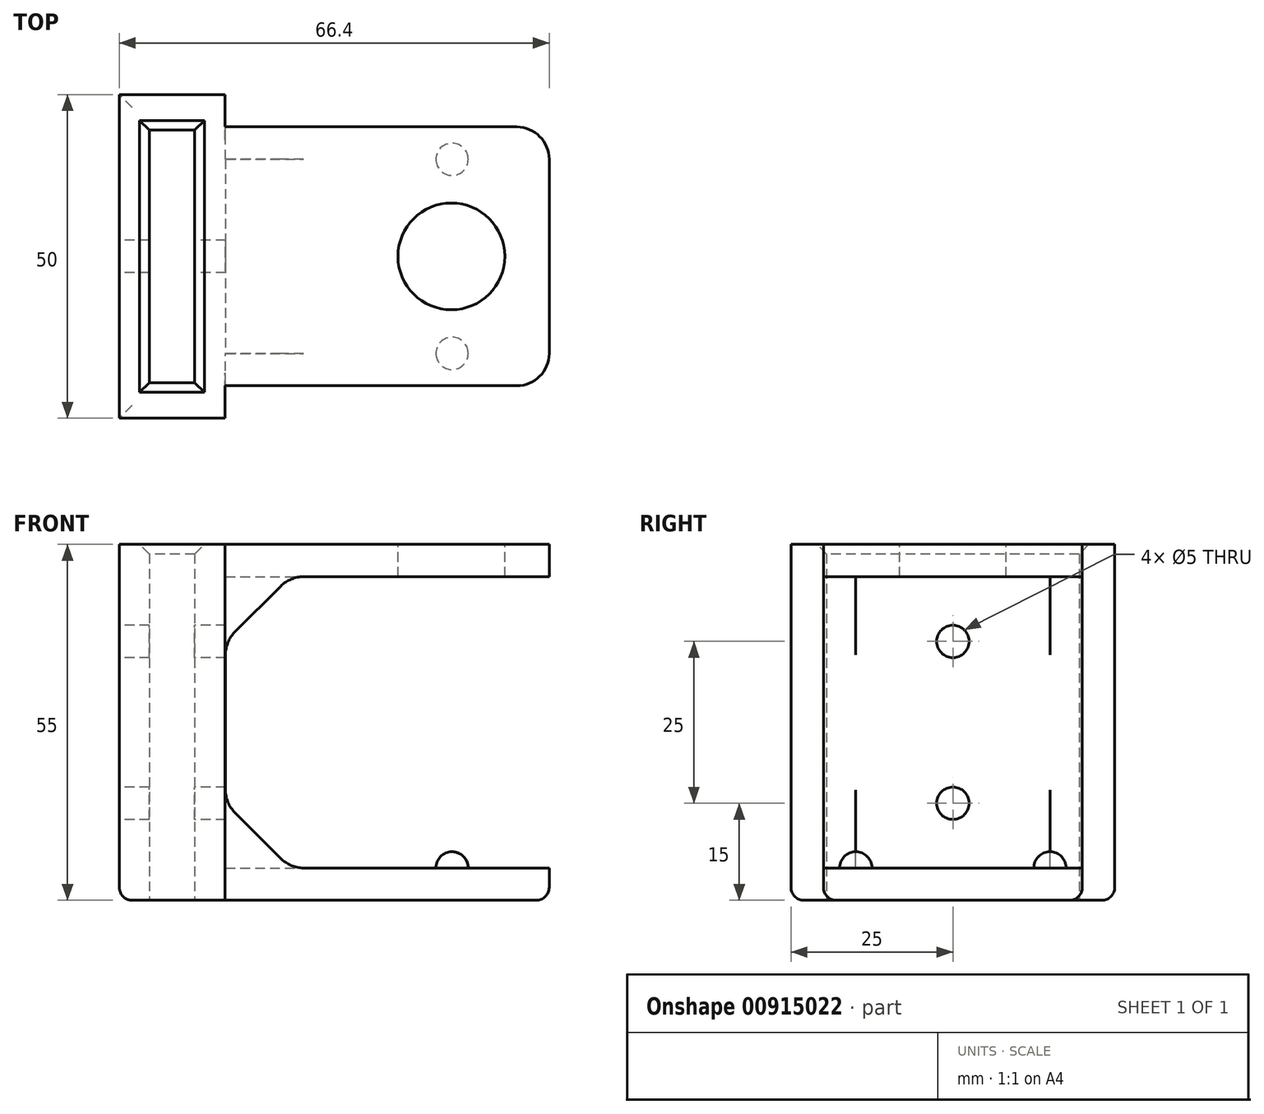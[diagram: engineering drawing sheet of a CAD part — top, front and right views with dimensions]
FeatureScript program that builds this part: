
annotation { "Feature Type Name" : "Feature", "Feature Type Description" : "" }
export const myFeature = defineFeature(function(context is Context, id is Id, definition is map)
    precondition{}
    {
        {
            var Q0;
            Q0=qCreatedBy(makeId("Front.planeOp"),FACE);
            var sketch = newSketch(context, id + "F0", { "sketchPlane" : qUnion([Q0])});
            skLineSegment(sketch, "E0", {"start": v(0, 0) * mm, "end": v(0, 55) * mm});
            skLineSegment(sketch, "E1", {"start": v(0, 55) * mm, "end": v(50.1, 55) * mm});
            skLineSegment(sketch, "E2", {"start": v(50.1, 55) * mm, "end": v(50.1, 50) * mm});
            skLineSegment(sketch, "E3", {"start": v(50.1, 50) * mm, "end": v(0.1, 50) * mm});
            skLineSegment(sketch, "E4", {"start": v(0.1, 50) * mm, "end": v(0.1, 5) * mm});
            skLineSegment(sketch, "E5", {"start": v(0.1, 5) * mm, "end": v(50.1, 5) * mm});
            skLineSegment(sketch, "E6", {"start": v(50.1, 5) * mm, "end": v(50.1, 0) * mm});
            skLineSegment(sketch, "E7", {"start": v(50.1, 0) * mm, "end": v(0, 0) * mm});
            skSolve(sketch);
        }
        {
            var Q0;
            Q0=makeQuery(id+"F0.imprint","IMPRINT",FACE,{"disambiguationData":[TD([[makeQuery(id+"F0.imprint","IMPRINT",EDGE,{"derivedFrom":sQuery(id+"F0.wireOp",EDGE,"E0")}),-1.0]])]});
            extrude(context, id + "F1", {"entities" : qUnion([Q0]), "oppositeDirection" : true, "depth" : 40 * mm, "offsetDistance" : 25 * mm});
        }
        {
            var Q0;
            Q0=makeQuery(id+"F1.opExtrude","SWEPT_FACE",FACE,{"disambiguationData":[OSD([sQuery(id+"F0.wireOp",EDGE,"E1")])]});
            var sketch = newSketch(context, id + "F2", { "sketchPlane" : qUnion([Q0])});
            skCircle(sketch, "E8", {"center": v(35, 20) * mm, "radius": 8.25 * mm});
            skPoint(sketch, "E8.centerSnap0", {"position": v(0, 20) * mm});
            skPoint(sketch, "E8.centerSnap1", {"position": v(25.05, 0) * mm});
            skSolve(sketch);
        }
        {
            var Q0;
            Q0=makeQuery(id+"F2.imprint","IMPRINT",FACE,{"disambiguationData":[TD([[makeQuery(id+"F2.imprint","IMPRINT",EDGE,{"derivedFrom":sQuery(id+"F2.wireOp",EDGE,"E8")}),1.0]])]});
            extrude(context, id + "F3", {"entities" : qUnion([Q0]), "operationType" : NewBodyOperationType.REMOVE, "endBound" : BoundingType.UP_TO_NEXT, "oppositeDirection" : true, "depth" : 25 * mm, "offsetDistance" : 25 * mm});
        }
        {
            var Q0;
            Q0=makeQuery(id+"F1.opExtrude","SWEPT_FACE",FACE,{"disambiguationData":[OSD([sQuery(id+"F0.wireOp",EDGE,"E0")])]});
            var sketch = newSketch(context, id + "F4", { "sketchPlane" : qUnion([Q0])});
            skLineSegment(sketch, "E9.bottom", {"start": v(5, 55) * mm, "end": v(-45, 55) * mm});
            skLineSegment(sketch, "E9.top", {"start": v(5, 0) * mm, "end": v(-45, 0) * mm});
            skLineSegment(sketch, "E9.left", {"start": v(5, 55) * mm, "end": v(5, 0) * mm});
            skLineSegment(sketch, "E9.right", {"start": v(-45, 55) * mm, "end": v(-45, 0) * mm});
            skPoint(sketch, "E9.middle", {"position": v(-20, 27.5) * mm});
            skPoint(sketch, "E9.middle.positionSnap0", {"position": v(-20, 55) * mm});
            skPoint(sketch, "E9.middle.positionSnap1", {"position": v(0, 27.5) * mm});
            skPoint(sketch, "E9.cornerSnap0", {"position": v(-20, 55) * mm});
            skPoint(sketch, "E9.centerSnap0", {"position": v(-20, 55) * mm});
            skPoint(sketch, "E9.centerSnap1", {"position": v(0, 27.5) * mm});
            skSolve(sketch);
        }
        {
            var Q0;
            {var subQ2=sQuery(id+"F4.wireOp",EDGE,"E9.left");Q0=makeQuery(id+"F4.imprint","IMPRINT",FACE,{"disambiguationData":[TD([[makeQuery(id+"F4.imprint","IMPRINT",EDGE,{"derivedFrom":subQ2}),-1.0]])]});}
            var Q1;
            {var subQ1=sQuery(id+"F0.wireOp",EDGE,"E0");var subQ2=makeQuery(id+"F1.opExtrude","CAP_EDGE",EDGE,{"disambiguationData":[OSD([subQ1])],"isStart":true});Q1=makeQuery(id+"F4.imprint","IMPRINT",FACE,{"disambiguationData":[TD([[makeQuery(id+"F4.imprint","IMPRINT",EDGE,{"derivedFrom":subQ2}),1.0]])]});}
            var Q2;
            {var subQ2=sQuery(id+"F4.wireOp",EDGE,"E9.right");Q2=makeQuery(id+"F4.imprint","IMPRINT",FACE,{"disambiguationData":[TD([[makeQuery(id+"F4.imprint","IMPRINT",EDGE,{"derivedFrom":subQ2}),1.0]])]});}
            extrude(context, id + "F5", {"entities" : qUnion([Q0, Q1, Q2]), "operationType" : NewBodyOperationType.ADD, "depth" : 16.3 * mm, "offsetDistance" : 25 * mm});
        }
        {
            var Q0;
            Q0=makeQuery(id+"F5.boolean.opBoolean","MERGE",FACE,{"derivedFrom":[makeQuery(id+"F1.opExtrude","SWEPT_FACE",FACE,{"disambiguationData":[OSD([sQuery(id+"F0.wireOp",EDGE,"E7")])]}),makeQuery(id+"F5.opExtrude","SWEPT_FACE",FACE,{"disambiguationData":[OSD([sQuery(id+"F4.wireOp",EDGE,"E9.top")])]})]});
            var sketch = newSketch(context, id + "F6", { "sketchPlane" : qUnion([Q0])});
            skLineSegment(sketch, "E10", {"start": v(0, 0) * mm, "end": v(0, -40) * mm, "construction": true});
            skLineSegment(sketch, "E11.bottom", {"start": v(-11.65, -39.5) * mm, "end": v(-4.65, -39.5) * mm});
            skLineSegment(sketch, "E11.top", {"start": v(-11.65, -0.5) * mm, "end": v(-4.65, -0.5) * mm});
            skLineSegment(sketch, "E11.left", {"start": v(-11.65, -39.5) * mm, "end": v(-11.65, -0.5) * mm});
            skLineSegment(sketch, "E11.right", {"start": v(-4.65, -39.5) * mm, "end": v(-4.65, -0.5) * mm});
            skPoint(sketch, "E11.middle", {"position": v(-8.15, -20) * mm});
            skPoint(sketch, "E11.middle.positionSnap0", {"position": v(-8.15, 5) * mm});
            skPoint(sketch, "E11.middle.positionSnap1", {"position": v(0, -20) * mm});
            skPoint(sketch, "E11.centerSnap0", {"position": v(-8.15, 5) * mm});
            skPoint(sketch, "E11.centerSnap1", {"position": v(0, -20) * mm});
            skSolve(sketch);
        }
        {
            var Q0;
            Q0=makeQuery(id+"F6.imprint","IMPRINT",FACE,{"disambiguationData":[TD([[makeQuery(id+"F6.imprint","IMPRINT",EDGE,{"derivedFrom":sQuery(id+"F6.wireOp",EDGE,"E11.bottom")}),1.0]])]});
            extrude(context, id + "F7", {"entities" : qUnion([Q0]), "operationType" : NewBodyOperationType.REMOVE, "endBound" : BoundingType.THROUGH_ALL, "oppositeDirection" : true, "depth" : 50 * mm, "offsetDistance" : 25 * mm});
        }
        {
            var Q0;
            Q0=makeQuery(id+"F1.opExtrude","SWEPT_EDGE",EDGE,{"disambiguationData":[OSD([sQuery(id+"F0.wireOp",EDGE,"E4"),sQuery(id+"F0.wireOp",EDGE,"E5")])]});
            var Q1;
            Q1=makeQuery(id+"F1.opExtrude","SWEPT_EDGE",EDGE,{"disambiguationData":[OSD([sQuery(id+"F0.wireOp",EDGE,"E3"),sQuery(id+"F0.wireOp",EDGE,"E4")])]});
            chamfer(context, id + "F8", {"entities" : qUnion([Q0, Q1]), "width" : 10 * mm, "tangentPropagation" : true});
        }
        {
            var Q0;
            Q0=makeQuery(id+"F5.opExtrude","CAP_FACE",FACE,{"disambiguationData":[OSD([sQuery(id+"F4.wireOp",EDGE,"E9.bottom"),sQuery(id+"F4.wireOp",EDGE,"E9.top"),sQuery(id+"F4.wireOp",EDGE,"E9.left"),sQuery(id+"F4.wireOp",EDGE,"E9.right")])],"isStart":false});
            var sketch = newSketch(context, id + "F9", { "sketchPlane" : qUnion([Q0])});
            skCircle(sketch, "E12", {"center": v(-20, 15) * mm, "radius": 2.5 * mm});
            skPoint(sketch, "E12.centerSnap0", {"position": v(-20, 0) * mm});
            skCircle(sketch, "E13", {"center": v(-20, 40) * mm, "radius": 2.5 * mm});
            skSolve(sketch);
        }
        {
            var Q0;
            Q0=makeQuery(id+"F9.imprint","IMPRINT",FACE,{"disambiguationData":[TD([[makeQuery(id+"F9.imprint","IMPRINT",EDGE,{"derivedFrom":sQuery(id+"F9.wireOp",EDGE,"E12")}),1.0]])]});
            var Q1;
            Q1=makeQuery(id+"F9.imprint","IMPRINT",FACE,{"disambiguationData":[TD([[makeQuery(id+"F9.imprint","IMPRINT",EDGE,{"derivedFrom":sQuery(id+"F9.wireOp",EDGE,"E13")}),1.0]])]});
            extrude(context, id + "F10", {"entities" : qUnion([Q0, Q1]), "operationType" : NewBodyOperationType.REMOVE, "endBound" : BoundingType.THROUGH_ALL, "oppositeDirection" : true, "depth" : 25 * mm, "offsetDistance" : 25 * mm});
        }
        {
            var Q0;
            Q0=makeQuery(id+"F1.opExtrude","SWEPT_FACE",FACE,{"disambiguationData":[OSD([sQuery(id+"F0.wireOp",EDGE,"E6")])]});
            var sketch = newSketch(context, id + "F11", { "sketchPlane" : qUnion([Q0])});
            skLineSegment(sketch, "E14.bottom", {"start": v(35, 5) * mm, "end": v(5, 5) * mm});
            skLineSegment(sketch, "E14.top", {"start": v(35, 15) * mm, "end": v(5, 15) * mm});
            skLineSegment(sketch, "E14.left", {"start": v(35, 5) * mm, "end": v(35, 15) * mm});
            skLineSegment(sketch, "E14.right", {"start": v(5, 5) * mm, "end": v(5, 15) * mm});
            skSolve(sketch);
        }
        {
            var Q0;
            Q0=makeQuery(id+"F11.imprint","IMPRINT",FACE,{"disambiguationData":[TD([[makeQuery(id+"F11.imprint","IMPRINT",EDGE,{"derivedFrom":sQuery(id+"F11.wireOp",EDGE,"E14.bottom")}),-1.0]])]});
            extrude(context, id + "F12", {"entities" : qUnion([Q0]), "operationType" : NewBodyOperationType.REMOVE, "oppositeDirection" : true, "depth" : 50 * mm, "offsetDistance" : 25 * mm});
        }
        {
            var Q0;
            Q0=makeQuery(id+"F1.opExtrude","SWEPT_FACE",FACE,{"disambiguationData":[OSD([sQuery(id+"F0.wireOp",EDGE,"E2")])]});
            var sketch = newSketch(context, id + "F13", { "sketchPlane" : qUnion([Q0])});
            skLineSegment(sketch, "E15.bottom", {"start": v(35, 50) * mm, "end": v(5, 50) * mm});
            skLineSegment(sketch, "E15.top", {"start": v(35, 40) * mm, "end": v(5, 40) * mm});
            skLineSegment(sketch, "E15.left", {"start": v(35, 50) * mm, "end": v(35, 40) * mm});
            skLineSegment(sketch, "E15.right", {"start": v(5, 50) * mm, "end": v(5, 40) * mm});
            skSolve(sketch);
        }
        {
            var Q0;
            Q0=makeQuery(id+"F13.imprint","IMPRINT",FACE,{"disambiguationData":[TD([[makeQuery(id+"F13.imprint","IMPRINT",EDGE,{"derivedFrom":sQuery(id+"F13.wireOp",EDGE,"E15.bottom")}),1.0]])]});
            extrude(context, id + "F14", {"entities" : qUnion([Q0]), "operationType" : NewBodyOperationType.REMOVE, "oppositeDirection" : true, "depth" : 50 * mm, "offsetDistance" : 25 * mm});
        }
        {
            var Q0;
            Q0=makeQuery(id+"F7.boolean.opBoolean","INTERSECT",EDGE,{"derivedFrom":[makeQuery(id+"F5.boolean.opBoolean","MERGE",FACE,{"derivedFrom":[makeQuery(id+"F1.opExtrude","SWEPT_FACE",FACE,{"disambiguationData":[OSD([sQuery(id+"F0.wireOp",EDGE,"E1")])]}),makeQuery(id+"F5.opExtrude","SWEPT_FACE",FACE,{"disambiguationData":[OSD([sQuery(id+"F4.wireOp",EDGE,"E9.bottom")])]})]}),makeQuery(id+"F7.opExtrude","SWEPT_FACE",FACE,{"disambiguationData":[OSD([sQuery(id+"F6.wireOp",EDGE,"E11.left")])]})]});
            var Q1;
            Q1=makeQuery(id+"F7.boolean.opBoolean","INTERSECT",EDGE,{"derivedFrom":[makeQuery(id+"F5.boolean.opBoolean","MERGE",FACE,{"derivedFrom":[makeQuery(id+"F1.opExtrude","SWEPT_FACE",FACE,{"disambiguationData":[OSD([sQuery(id+"F0.wireOp",EDGE,"E1")])]}),makeQuery(id+"F5.opExtrude","SWEPT_FACE",FACE,{"disambiguationData":[OSD([sQuery(id+"F4.wireOp",EDGE,"E9.bottom")])]})]}),makeQuery(id+"F7.opExtrude","SWEPT_FACE",FACE,{"disambiguationData":[OSD([sQuery(id+"F6.wireOp",EDGE,"E11.bottom")])]})]});
            var Q2;
            Q2=makeQuery(id+"F7.boolean.opBoolean","INTERSECT",EDGE,{"derivedFrom":[makeQuery(id+"F5.boolean.opBoolean","MERGE",FACE,{"derivedFrom":[makeQuery(id+"F1.opExtrude","SWEPT_FACE",FACE,{"disambiguationData":[OSD([sQuery(id+"F0.wireOp",EDGE,"E1")])]}),makeQuery(id+"F5.opExtrude","SWEPT_FACE",FACE,{"disambiguationData":[OSD([sQuery(id+"F4.wireOp",EDGE,"E9.bottom")])]})]}),makeQuery(id+"F7.opExtrude","SWEPT_FACE",FACE,{"disambiguationData":[OSD([sQuery(id+"F6.wireOp",EDGE,"E11.right")])]})]});
            var Q3;
            Q3=makeQuery(id+"F7.boolean.opBoolean","INTERSECT",EDGE,{"derivedFrom":[makeQuery(id+"F5.boolean.opBoolean","MERGE",FACE,{"derivedFrom":[makeQuery(id+"F1.opExtrude","SWEPT_FACE",FACE,{"disambiguationData":[OSD([sQuery(id+"F0.wireOp",EDGE,"E1")])]}),makeQuery(id+"F5.opExtrude","SWEPT_FACE",FACE,{"disambiguationData":[OSD([sQuery(id+"F4.wireOp",EDGE,"E9.bottom")])]})]}),makeQuery(id+"F7.opExtrude","SWEPT_FACE",FACE,{"disambiguationData":[OSD([sQuery(id+"F6.wireOp",EDGE,"E11.top")])]})]});
            var Q4;
            Q4=makeQuery(id+"F7.boolean.opBoolean","COPY",EDGE,{"derivedFrom":makeQuery(id+"F7.opExtrude","CAP_EDGE",EDGE,{"disambiguationData":[OSD([sQuery(id+"F6.wireOp",EDGE,"E11.left")])],"isStart":true})});
            var Q5;
            Q5=makeQuery(id+"F7.boolean.opBoolean","COPY",EDGE,{"derivedFrom":makeQuery(id+"F7.opExtrude","CAP_EDGE",EDGE,{"disambiguationData":[OSD([sQuery(id+"F6.wireOp",EDGE,"E11.top")])],"isStart":true})});
            var Q6;
            Q6=makeQuery(id+"F7.boolean.opBoolean","COPY",EDGE,{"derivedFrom":makeQuery(id+"F7.opExtrude","CAP_EDGE",EDGE,{"disambiguationData":[OSD([sQuery(id+"F6.wireOp",EDGE,"E11.right")])],"isStart":true})});
            var Q7;
            Q7=makeQuery(id+"F7.boolean.opBoolean","COPY",EDGE,{"derivedFrom":makeQuery(id+"F7.opExtrude","CAP_EDGE",EDGE,{"disambiguationData":[OSD([sQuery(id+"F6.wireOp",EDGE,"E11.bottom")])],"isStart":true})});
            chamfer(context, id + "F15", {"entities" : qUnion([Q0, Q1, Q2, Q3, Q4, Q5, Q6, Q7]), "width" : 1.5 * mm, "tangentPropagation" : true});
        }
        {
            var Q0;
            Q0=makeQuery(id+"F1.opExtrude","CAP_EDGE",EDGE,{"disambiguationData":[OSD([sQuery(id+"F0.wireOp",EDGE,"E2")])],"isStart":true});
            var Q1;
            Q1=makeQuery(id+"F1.opExtrude","CAP_EDGE",EDGE,{"disambiguationData":[OSD([sQuery(id+"F0.wireOp",EDGE,"E2")])],"isStart":false});
            var Q2;
            Q2=makeQuery(id+"F1.opExtrude","CAP_EDGE",EDGE,{"disambiguationData":[OSD([sQuery(id+"F0.wireOp",EDGE,"E6")])],"isStart":false});
            var Q3;
            Q3=makeQuery(id+"F1.opExtrude","CAP_EDGE",EDGE,{"disambiguationData":[OSD([sQuery(id+"F0.wireOp",EDGE,"E6")])],"isStart":true});
            var Q4;
            {var subQ0=sQuery(id+"F0.wireOp",EDGE,"E5");var subQ1=sQuery(id+"F0.wireOp",EDGE,"E4");var subQ2=makeQuery(id+"F1.opExtrude","SWEPT_FACE",FACE,{"disambiguationData":[OSD([subQ1])]});Q4=makeQuery(id+"F10.boolean.opBoolean","SPLIT",EDGE,{"disambiguationData":[TD([makeQuery(id+"F1.opExtrude","CAP_FACE",FACE,{"disambiguationData":[OSD([sQuery(id+"F0.wireOp",EDGE,"E0"),sQuery(id+"F0.wireOp",EDGE,"E1"),sQuery(id+"F0.wireOp",EDGE,"E2"),sQuery(id+"F0.wireOp",EDGE,"E3"),subQ1,subQ0,sQuery(id+"F0.wireOp",EDGE,"E6"),sQuery(id+"F0.wireOp",EDGE,"E7")])],"isStart":false})])],"derivedFrom":makeQuery(id+"F8.opChamfer","BLEND_EDGE",EDGE,{"blendedFrom":[makeQuery(id+"F1.opExtrude","SWEPT_EDGE",EDGE,{"disambiguationData":[OSD([subQ1,subQ0])]}),subQ2],"blendedInto":[subQ2]})});}
            var Q5;
            {var subQ0=sQuery(id+"F0.wireOp",EDGE,"E5");var subQ1=sQuery(id+"F0.wireOp",EDGE,"E4");var subQ2=makeQuery(id+"F1.opExtrude","SWEPT_FACE",FACE,{"disambiguationData":[OSD([subQ1])]});Q5=makeQuery(id+"F10.boolean.opBoolean","SPLIT",EDGE,{"disambiguationData":[TD([makeQuery(id+"F1.opExtrude","CAP_FACE",FACE,{"disambiguationData":[OSD([sQuery(id+"F0.wireOp",EDGE,"E0"),sQuery(id+"F0.wireOp",EDGE,"E1"),sQuery(id+"F0.wireOp",EDGE,"E2"),sQuery(id+"F0.wireOp",EDGE,"E3"),subQ1,subQ0,sQuery(id+"F0.wireOp",EDGE,"E6"),sQuery(id+"F0.wireOp",EDGE,"E7")])],"isStart":true})])],"derivedFrom":makeQuery(id+"F8.opChamfer","BLEND_EDGE",EDGE,{"blendedFrom":[makeQuery(id+"F1.opExtrude","SWEPT_EDGE",EDGE,{"disambiguationData":[OSD([subQ1,subQ0])]}),subQ2],"blendedInto":[subQ2]})});}
            var Q6;
            {var subQ0=sQuery(id+"F0.wireOp",EDGE,"E5");var subQ1=sQuery(id+"F0.wireOp",EDGE,"E4");var subQ2=makeQuery(id+"F1.opExtrude","SWEPT_FACE",FACE,{"disambiguationData":[OSD([subQ0])]});Q6=makeQuery(id+"F12.boolean.opBoolean","SPLIT",EDGE,{"disambiguationData":[TD([makeQuery(id+"F12.opExtrude","SWEPT_FACE",FACE,{"disambiguationData":[OSD([sQuery(id+"F11.wireOp",EDGE,"E14.right")])]})])],"derivedFrom":makeQuery(id+"F8.opChamfer","BLEND_EDGE",EDGE,{"blendedFrom":[makeQuery(id+"F1.opExtrude","SWEPT_EDGE",EDGE,{"disambiguationData":[OSD([subQ1,subQ0])]}),subQ2],"blendedInto":[subQ2]})});}
            var Q7;
            {var subQ0=sQuery(id+"F0.wireOp",EDGE,"E5");var subQ1=sQuery(id+"F0.wireOp",EDGE,"E4");var subQ2=makeQuery(id+"F1.opExtrude","SWEPT_FACE",FACE,{"disambiguationData":[OSD([subQ0])]});Q7=makeQuery(id+"F12.boolean.opBoolean","SPLIT",EDGE,{"disambiguationData":[TD([makeQuery(id+"F12.opExtrude","SWEPT_FACE",FACE,{"disambiguationData":[OSD([sQuery(id+"F11.wireOp",EDGE,"E14.left")])]})])],"derivedFrom":makeQuery(id+"F8.opChamfer","BLEND_EDGE",EDGE,{"blendedFrom":[makeQuery(id+"F1.opExtrude","SWEPT_EDGE",EDGE,{"disambiguationData":[OSD([subQ1,subQ0])]}),subQ2],"blendedInto":[subQ2]})});}
            var Q8;
            {var subQ0=sQuery(id+"F0.wireOp",EDGE,"E4");var subQ1=sQuery(id+"F0.wireOp",EDGE,"E3");var subQ2=makeQuery(id+"F1.opExtrude","SWEPT_FACE",FACE,{"disambiguationData":[OSD([subQ0])]});Q8=makeQuery(id+"F10.boolean.opBoolean","SPLIT",EDGE,{"disambiguationData":[TD([makeQuery(id+"F1.opExtrude","CAP_FACE",FACE,{"disambiguationData":[OSD([sQuery(id+"F0.wireOp",EDGE,"E0"),sQuery(id+"F0.wireOp",EDGE,"E1"),sQuery(id+"F0.wireOp",EDGE,"E2"),subQ1,subQ0,sQuery(id+"F0.wireOp",EDGE,"E5"),sQuery(id+"F0.wireOp",EDGE,"E6"),sQuery(id+"F0.wireOp",EDGE,"E7")])],"isStart":true})])],"derivedFrom":makeQuery(id+"F8.opChamfer","BLEND_EDGE",EDGE,{"blendedFrom":[makeQuery(id+"F1.opExtrude","SWEPT_EDGE",EDGE,{"disambiguationData":[OSD([subQ1,subQ0])]}),subQ2],"blendedInto":[subQ2]})});}
            var Q9;
            {var subQ0=sQuery(id+"F0.wireOp",EDGE,"E4");var subQ1=sQuery(id+"F0.wireOp",EDGE,"E3");var subQ2=makeQuery(id+"F1.opExtrude","SWEPT_FACE",FACE,{"disambiguationData":[OSD([subQ0])]});Q9=makeQuery(id+"F10.boolean.opBoolean","SPLIT",EDGE,{"disambiguationData":[TD([makeQuery(id+"F1.opExtrude","CAP_FACE",FACE,{"disambiguationData":[OSD([sQuery(id+"F0.wireOp",EDGE,"E0"),sQuery(id+"F0.wireOp",EDGE,"E1"),sQuery(id+"F0.wireOp",EDGE,"E2"),subQ1,subQ0,sQuery(id+"F0.wireOp",EDGE,"E5"),sQuery(id+"F0.wireOp",EDGE,"E6"),sQuery(id+"F0.wireOp",EDGE,"E7")])],"isStart":false})])],"derivedFrom":makeQuery(id+"F8.opChamfer","BLEND_EDGE",EDGE,{"blendedFrom":[makeQuery(id+"F1.opExtrude","SWEPT_EDGE",EDGE,{"disambiguationData":[OSD([subQ1,subQ0])]}),subQ2],"blendedInto":[subQ2]})});}
            var Q10;
            {var subQ0=sQuery(id+"F0.wireOp",EDGE,"E4");var subQ1=sQuery(id+"F0.wireOp",EDGE,"E3");var subQ2=makeQuery(id+"F1.opExtrude","SWEPT_FACE",FACE,{"disambiguationData":[OSD([subQ1])]});Q10=makeQuery(id+"F14.boolean.opBoolean","SPLIT",EDGE,{"disambiguationData":[TD([makeQuery(id+"F14.opExtrude","SWEPT_FACE",FACE,{"disambiguationData":[OSD([sQuery(id+"F13.wireOp",EDGE,"E15.left")])]})])],"derivedFrom":makeQuery(id+"F8.opChamfer","BLEND_EDGE",EDGE,{"blendedFrom":[makeQuery(id+"F1.opExtrude","SWEPT_EDGE",EDGE,{"disambiguationData":[OSD([subQ1,subQ0])]}),subQ2],"blendedInto":[subQ2]})});}
            var Q11;
            {var subQ0=sQuery(id+"F0.wireOp",EDGE,"E4");var subQ1=sQuery(id+"F0.wireOp",EDGE,"E3");var subQ2=makeQuery(id+"F1.opExtrude","SWEPT_FACE",FACE,{"disambiguationData":[OSD([subQ1])]});Q11=makeQuery(id+"F14.boolean.opBoolean","SPLIT",EDGE,{"disambiguationData":[TD([makeQuery(id+"F14.opExtrude","SWEPT_FACE",FACE,{"disambiguationData":[OSD([sQuery(id+"F13.wireOp",EDGE,"E15.right")])]})])],"derivedFrom":makeQuery(id+"F8.opChamfer","BLEND_EDGE",EDGE,{"blendedFrom":[makeQuery(id+"F1.opExtrude","SWEPT_EDGE",EDGE,{"disambiguationData":[OSD([subQ1,subQ0])]}),subQ2],"blendedInto":[subQ2]})});}
            fillet(context, id + "F16", {"entities" : qUnion([Q0, Q1, Q2, Q3, Q4, Q5, Q6, Q7, Q8, Q9, Q10, Q11]), "radius" : 5 * mm, "tangentPropagation" : true, "allowEdgeOverflow" : false});
        }
        {
            var Q0;
            Q0=makeQuery(id+"F12.boolean.opBoolean","MERGE",FACE,{"derivedFrom":[makeQuery(id+"F1.opExtrude","SWEPT_FACE",FACE,{"disambiguationData":[OSD([sQuery(id+"F0.wireOp",EDGE,"E5")])]})],"fromTools":[makeQuery(id+"F12.opExtrude","SWEPT_FACE",FACE,{"disambiguationData":[OSD([sQuery(id+"F11.wireOp",EDGE,"E14.bottom")])]})]});
            var sketch = newSketch(context, id + "F17", { "sketchPlane" : qUnion([Q0])});
            skCircle(sketch, "E16", {"center": v(35.1, 5) * mm, "radius": 2.5 * mm});
            skCircle(sketch, "E17", {"center": v(35.1, 35) * mm, "radius": 2.5 * mm});
            skSolve(sketch);
        }
        {
            var Q0;
            Q0=makeQuery(id+"F17.imprint","IMPRINT",FACE,{"disambiguationData":[TD([[makeQuery(id+"F17.imprint","IMPRINT",EDGE,{"derivedFrom":sQuery(id+"F17.wireOp",EDGE,"E16")}),1.0]])]});
            var Q1;
            Q1=makeQuery(id+"F17.imprint","IMPRINT",FACE,{"disambiguationData":[TD([[makeQuery(id+"F17.imprint","IMPRINT",EDGE,{"derivedFrom":sQuery(id+"F17.wireOp",EDGE,"E17")}),1.0]])]});
            var Q2;
            Q2=makeQuery(id+"F17.imprint","IMPRINT",FACE,{"disambiguationData":[TD([[makeQuery(id+"F17.imprint","IMPRINT",EDGE,{"derivedFrom":sQuery(id+"F17.wireOp",EDGE,"mlo0WZYm-0syK-0T6o-3RNE-c6q9ZTtoNqkQ")}),1.0]])]});
            var Q3;
            Q3=makeQuery(id+"F17.imprint","IMPRINT",FACE,{"disambiguationData":[TD([[makeQuery(id+"F17.imprint","IMPRINT",EDGE,{"derivedFrom":sQuery(id+"F17.wireOp",EDGE,"KuUrXkiH-Sutg-maJh-nNTU-JfOtcmXtJkck")}),1.0]])]});
            extrude(context, id + "F18", {"entities" : qUnion([Q0, Q1, Q2, Q3]), "operationType" : NewBodyOperationType.ADD, "depth" : 2.5 * mm, "offsetDistance" : 25 * mm});
        }
        {
            var Q0;
            Q0=makeQuery(id+"F18.opExtrude","CAP_EDGE",EDGE,{"disambiguationData":[OSD([sQuery(id+"F17.wireOp",EDGE,"E16")])],"isStart":false});
            var Q1;
            Q1=makeQuery(id+"F18.opExtrude","CAP_EDGE",EDGE,{"disambiguationData":[OSD([sQuery(id+"F17.wireOp",EDGE,"E17")])],"isStart":false});
            var Q2;
            Q2=makeQuery(id+"F18.opExtrude","CAP_EDGE",EDGE,{"disambiguationData":[OSD([sQuery(id+"F17.wireOp",EDGE,"KuUrXkiH-Sutg-maJh-nNTU-JfOtcmXtJkck")])],"isStart":false});
            var Q3;
            Q3=makeQuery(id+"F18.opExtrude","CAP_EDGE",EDGE,{"disambiguationData":[OSD([sQuery(id+"F17.wireOp",EDGE,"mlo0WZYm-0syK-0T6o-3RNE-c6q9ZTtoNqkQ")])],"isStart":false});
            fillet(context, id + "F19", {"entities" : qUnion([Q0, Q1, Q2, Q3]), "radius" : 2.5 * mm, "tangentPropagation" : true, "allowEdgeOverflow" : false});
        }
        {
            var Q0;
            Q0=makeQuery(id+"F5.opExtrude","SWEPT_EDGE",EDGE,{"disambiguationData":[OSD([sQuery(id+"F4.wireOp",EDGE,"E9.top"),sQuery(id+"F4.wireOp",EDGE,"E9.left")])]});
            var Q1;
            Q1=makeQuery(id+"F5.opExtrude","SWEPT_EDGE",EDGE,{"disambiguationData":[OSD([sQuery(id+"F4.wireOp",EDGE,"E9.top"),sQuery(id+"F4.wireOp",EDGE,"E9.right")])]});
            var Q2;
            Q2=makeQuery(id+"F5.opExtrude","CAP_EDGE",EDGE,{"disambiguationData":[OSD([sQuery(id+"F4.wireOp",EDGE,"E9.top")])],"isStart":false});
            var Q3;
            Q3=makeQuery(id+"F1.opExtrude","CAP_EDGE",EDGE,{"disambiguationData":[OSD([sQuery(id+"F0.wireOp",EDGE,"E7")])],"isStart":false});
            fillet(context, id + "F20", {"entities" : qUnion([Q0, Q1, Q2, Q3]), "radius" : 2 * mm, "tangentPropagation" : true, "allowEdgeOverflow" : false});
        }
    });
